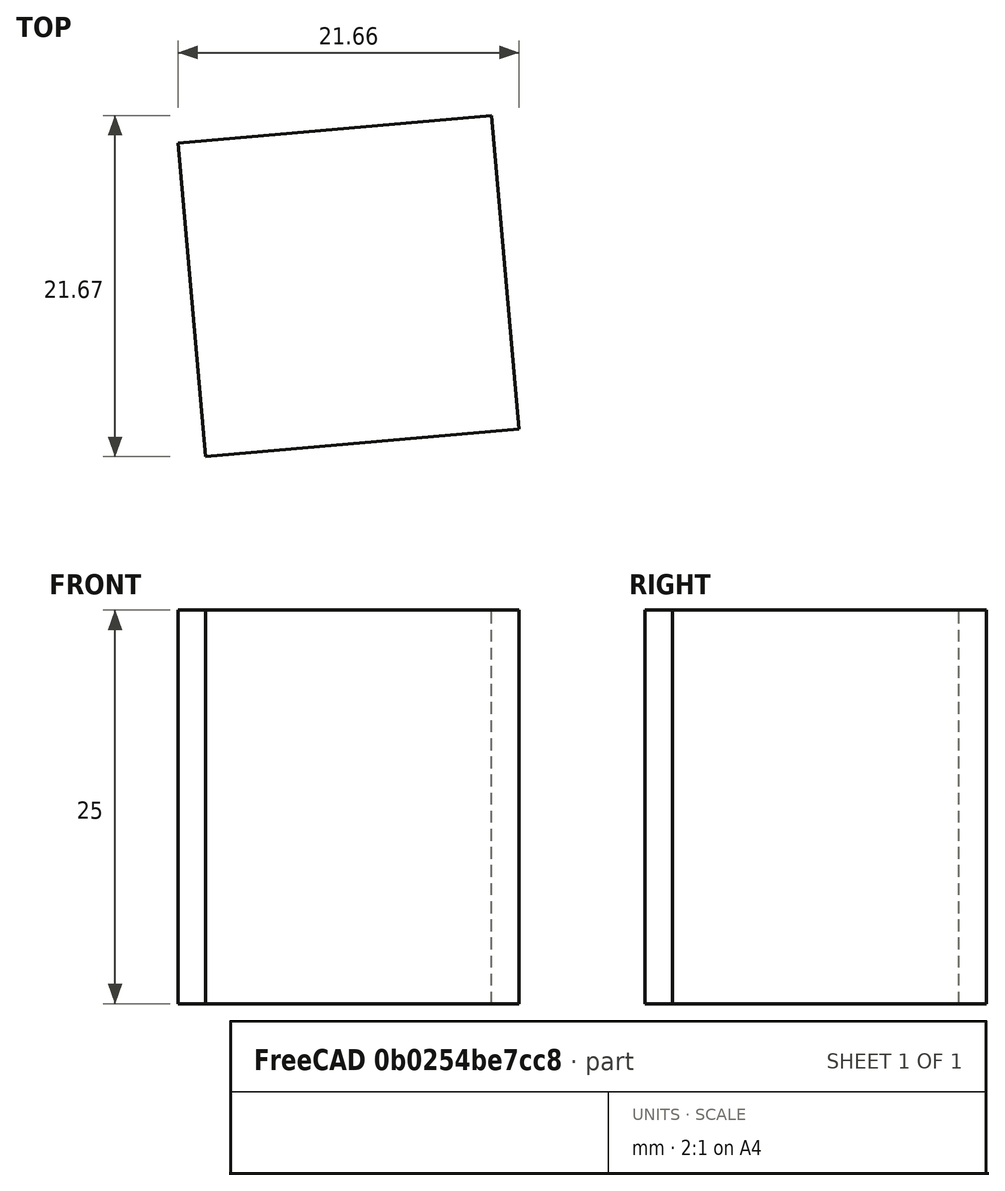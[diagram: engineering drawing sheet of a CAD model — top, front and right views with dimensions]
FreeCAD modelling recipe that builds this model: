
FCSTD DOCUMENT  (FreeCAD 0.19R24267 +99 (Git))
Label: Hopper_Modified
License: All rights reserved
LicenseURL: http://en.wikipedia.org/wiki/All_rights_reserved
objects: Part::Feature×2, PartDesign::FeatureBase×2, PartDesign::Body×2, Part::Box×1, Part::Compound×1
note: 8 computed .brp shape members not serialized (recipe doc carries the construction recipe); baked Part::Feature solids carry a one-line shape summary decoded from their .brp

FEATURE [Part::Feature] Hopper001
  shape: bbox 72.69 x 49.3 x 49.65 mm, 7488 faces, 0 solids (baked)
FEATURE [Part::Box] Box  label="Cube"
  AttacherType = Attacher::AttachEngine3D
  Height = 25
  Length = 20
  Placement = pos=(50.36,-0.99,12.5) rot=(0,0,1;0.087266rad)
  Width = 20
FEATURE [Part::Compound] Compound
  Links = -> [Box,Hopper001]
FEATURE [PartDesign::FeatureBase] BaseFeature
  BaseFeature = -> Compound
FEATURE [PartDesign::Body] Body
  BaseFeature = -> Compound
  Group = -> [BaseFeature]
  Origin = -> Origin
  Tip = -> BaseFeature
FEATURE [Part::Feature] Arm001
  Placement = pos=(27,2,20.5) rot=(0,0,1;0rad)
  shape: bbox 55.29 x 68.8 x 6.5 mm, 4786 faces, 0 solids (baked)
FEATURE [PartDesign::FeatureBase] BaseFeature001
  BaseFeature = -> Arm001
FEATURE [PartDesign::Body] Body001
  BaseFeature = -> Arm001
  Group = -> [BaseFeature001]
  Origin = -> Origin001
  Placement = pos=(27,2,20.5) rot=(0,0,1;0rad)
  Tip = -> BaseFeature001
